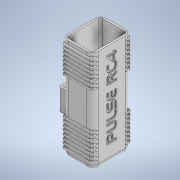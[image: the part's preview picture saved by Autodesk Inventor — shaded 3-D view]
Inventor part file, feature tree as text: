
AUTODESK INVENTOR PART (.ipt)
format: ipt  version: 2021 (Build 250183000, 183)  size: 1,136,640 bytes
history: native  units: mm
features: extrude x14, sketch x13, plane x7, mirror x6, fillet x6, projected_geometry x2, other x1
ambient origin geometry x8: Origin, YZ Plane, XZ Plane, XY Plane, X Axis, Y Axis, Z Axis, Center Point
bodies: Body1 (feature_tree)
feature tree (49):
  other  "Sólido1"
  extrude  "Extrusión1"  Depth=36.5mm
  extrude  "Extrusión2"  Depth=6.0mm
  extrude  "Extrusión3"  Depth=2.0mm
  plane  "Plano de trabajo1"
  mirror  "Simetría1"
  fillet  "Empalme1"  Radius=108.0mm
  plane  "Plano de trabajo2"
  extrude  "Extrusión4"  Depth=8.0mm
  plane  "Plano de trabajo3"
  mirror  "Simetría2"
  plane  "Plano de trabajo4"
  mirror  "Simetría3"
  plane  "Plano de trabajo5"
  mirror  "Simetría4"
  plane  "Plano de trabajo6"
  mirror  "Simetría5"
  plane  "Plano de trabajo8"
  mirror  "Simetría6"
  fillet  "Empalme2"  Radius=2.0mm
  fillet  "Empalme3"  Radius=2.0mm
  sketch  "Boceto4"  dims[d4=2.0mm d5=2.0mm d6=108.0mm d7=0.0mm]
  extrude  "Extrusión5"  Depth=2.0mm TaperAngle=0.0deg
  extrude  "Extrusión6"  Depth=6.0mm
  extrude  "Extrusión7"  Depth=11.0mm
  extrude  "Extrusión8"  [1 undecoded]
  extrude  "Extrusión9"  Depth=2.0mm
  fillet  "Empalme4"  Radius=2.0mm
  extrude  "Extrusión10"  [1 undecoded]
  extrude  "Extrusión11"  [1 undecoded]
  extrude  "Extrusión12"  Depth=1.0mm
  extrude  "Extrusión13"  Depth=20.0mm
  fillet  "Empalme6"  Radius=4.15mm
  extrude  "Extrusión14"  Depth=9.0mm
  fillet  "Empalme7"  Radius=24.0mm
  sketch  "Boceto2"  dims[d0=27.85mm d1=36.5mm]
  sketch  "Boceto3"  dims[d2=2.0mm d3=6.0mm]
  sketch  "Boceto5"  dims[d8=2.0mm d9=0.0mm d10=8.0mm d11=2.0mm d12=2.0mm]
  sketch  "Boceto6"  dims[d13=2.0mm d14=2.0mm d15=0.0mm]
  sketch  "Boceto7"  dims[d16=20.0mm d17=6.0mm]
  sketch  "Boceto8"  dims[d18=3.2mm d19=11.0mm]
  projected_geometry  "Contorno proyectado1"
  sketch  "Boceto9"  dims[d20=5.0mm d21=-4.0mm]
  sketch  "Boceto10"  dims[d22=1.0mm d23=2.0mm d24=2.0mm d25=0.0mm]
  sketch  "Boceto11"  dims[d26=-3.0mm d27=-4.0mm]
  sketch  "Boceto12"  dims[d28=-8.0mm d29=-33.5mm]
  sketch  "Boceto13"  dims[d30=1.0mm d31=1.0mm]
  projected_geometry  "Contorno proyectado2"
  sketch  "Boceto14"  dims[d32=1.0mm d33=0.0mm d37=20.0mm d38=4.15mm d39=4.35mm d40=24.0mm d41=14.0mm d42=0.0mm d43=8.0mm d44=0.0mm d45=7.0mm d46=2.0mm d47=15.0mm d48=0.0mm d49=2.0mm d50=7.0mm d51=0.0mm d52=2.0mm d53=6.0mm d54=0.0mm d56=14.0mm d57=0.0mm d58=8.0mm d59=0.0mm d60=8.0mm d61=0.0mm d62=2.0mm d63=8.0mm d64=0.0mm d65=75.0mm d66=75.0mm d67=16.5mm d68=11.273282mm d70=8.0mm d71=2.0mm d72=9.0mm d73=9.0mm]
note: 3 required parameter values undecoded (feature->parameter linkage not recoverable at this tier; creation-order binding heuristic only, values carry confidence <= 0.55)
